# Revit family: P200880KC-062c_KVUC606KSS
name_source: partatom
category: Specialty Equipment
units: mm (PartAtom-declared; Revit-internal decimal feet)

## family parameters
Always vertical = Yes
Cut with Voids When Loaded = No
Enable Cutting in Views = No
Maintain Annotation Orientation = No
Part Type = Normal
Room Calculation Point = No
Round Connector Dimension = Use Diameter
Shared = No
Work Plane-Based = No

## types (1)
- KVUC606KSS
    Amps = 0 A
    Body Material = ARCAT - Metal - Steel - Stainless
    Default Elevation = 0"
    Depth = 23"
    Description = 36" Commercial-Style Under-Cabinet Range Hood System, 585 CFM
36" Commercial-Style Under-Cabinet Range Hood System, 585 CFM
    Family Name = Ventilation
    Feature 1 = 585 CFM Motor Class Ventilation System
585 CFM Motor Class Ventilation System
    Feature 2 = 3-Speed Fan Control with Power Boost Function
3-Speed Fan Control with Power Boost Function
    Feature 3 = 90,0000 BTU Threshold
90,0000 BTU Threshold
    Grid Material = ARCAT - Metal - Light Gray
    Height = 10"
    Light Material = ARCAT - Glass - White
    Light Panel Material = ARCAT - Metal - Steel - Stainless Polished
    Manufacturer = KitchenAid
    Model = KVUC606KSS
    Switch Material = ARCAT - Metal - Steel - Stainless
    Voltage = 0 V
    Width = 36"

## geometry (parser evidence)
native form markers: Sweep x5
no freeform markers — native parametric forms only
